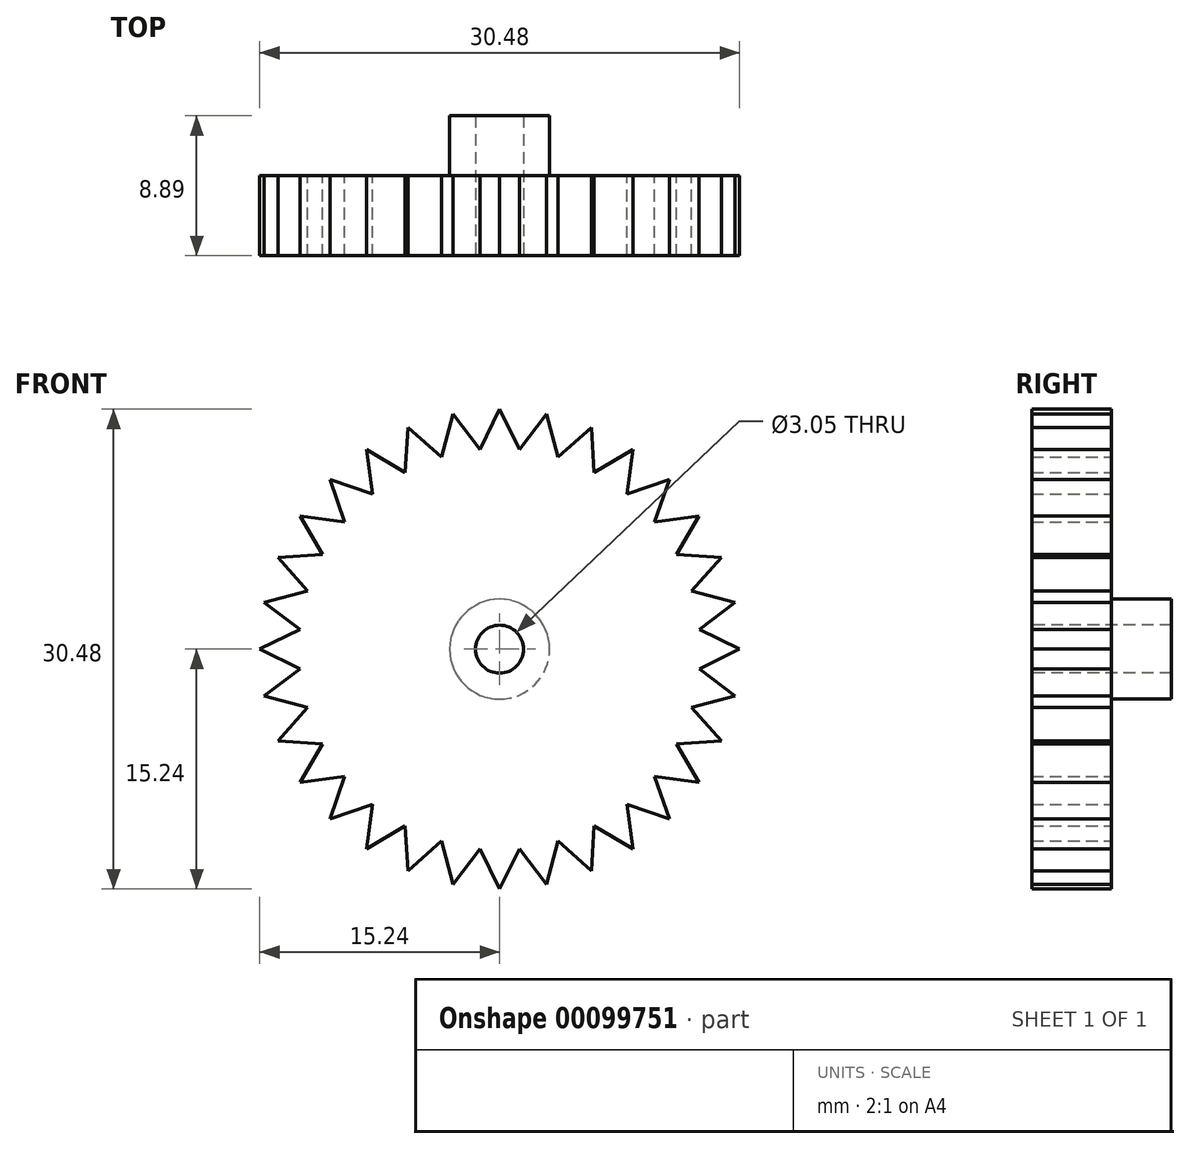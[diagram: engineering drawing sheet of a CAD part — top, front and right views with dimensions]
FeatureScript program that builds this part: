
annotation { "Feature Type Name" : "Feature", "Feature Type Description" : "" }
export const myFeature = defineFeature(function(context is Context, id is Id, definition is map)
    precondition{}
    {
        {
            var Q0;
            Q0=qCreatedBy(makeId("Front.planeOp"),FACE);
            var sketch = newSketch(context, id + "F0", { "sketchPlane" : qUnion([Q0])});
            skCircle(sketch, "E0", {"center": v(0, 0) * mm, "radius": 12.7 * mm});
            skLineSegment(sketch, "E1", {"start": v(1.27, 12.64) * mm, "end": v(0, 15.24) * mm});
            skLineSegment(sketch, "E2", {"start": v(0, 15.24) * mm, "end": v(-1.27, 12.64) * mm});
            skLineSegment(sketch, "E3.1.0", {"start": v(-2.97, 14.95) * mm, "end": v(-3.71, 12.15) * mm});
            skLineSegment(sketch, "E3.1.1", {"start": v(-1.22, 12.64) * mm, "end": v(-2.97, 14.95) * mm});
            skLineSegment(sketch, "E3.2.0", {"start": v(-5.83, 14.08) * mm, "end": v(-6, 11.19) * mm});
            skLineSegment(sketch, "E3.2.1", {"start": v(-3.66, 12.16) * mm, "end": v(-5.83, 14.08) * mm});
            skLineSegment(sketch, "E4.2.3.0", {"start": v(-8.47, 12.67) * mm, "end": v(-8.08, 9.8) * mm});
            skLineSegment(sketch, "E4.3.3.0", {"start": v(-5.96, 11.21) * mm, "end": v(-8.47, 12.67) * mm});
            skLineSegment(sketch, "E4.2.4.0", {"start": v(-10.78, 10.78) * mm, "end": v(-9.83, 8.04) * mm});
            skLineSegment(sketch, "E4.3.4.0", {"start": v(-8.04, 9.83) * mm, "end": v(-10.78, 10.78) * mm});
            skLineSegment(sketch, "E4.2.5.0", {"start": v(-12.67, 8.47) * mm, "end": v(-11.21, 5.96) * mm});
            skLineSegment(sketch, "E4.3.5.0", {"start": v(-9.8, 8.08) * mm, "end": v(-12.67, 8.47) * mm});
            skLineSegment(sketch, "E4.2.6.0", {"start": v(-14.08, 5.83) * mm, "end": v(-12.16, 3.66) * mm});
            skLineSegment(sketch, "E4.3.6.0", {"start": v(-11.19, 6) * mm, "end": v(-14.08, 5.83) * mm});
            skLineSegment(sketch, "E4.2.7.0", {"start": v(-14.95, 2.97) * mm, "end": v(-12.64, 1.22) * mm});
            skLineSegment(sketch, "E4.3.7.0", {"start": v(-12.15, 3.71) * mm, "end": v(-14.95, 2.97) * mm});
            skLineSegment(sketch, "E4.2.8.0", {"start": v(-15.24, 0) * mm, "end": v(-12.64, -1.27) * mm});
            skLineSegment(sketch, "E4.3.8.0", {"start": v(-12.64, 1.27) * mm, "end": v(-15.24, 0) * mm});
            skLineSegment(sketch, "E4.2.9.0", {"start": v(-14.95, -2.97) * mm, "end": v(-12.15, -3.71) * mm});
            skLineSegment(sketch, "E4.3.9.0", {"start": v(-12.64, -1.22) * mm, "end": v(-14.95, -2.97) * mm});
            skLineSegment(sketch, "E4.2.10.0", {"start": v(-14.08, -5.83) * mm, "end": v(-11.19, -6) * mm});
            skLineSegment(sketch, "E4.3.10.0", {"start": v(-12.16, -3.66) * mm, "end": v(-14.08, -5.83) * mm});
            skLineSegment(sketch, "E4.2.11.0", {"start": v(-12.67, -8.47) * mm, "end": v(-9.8, -8.08) * mm});
            skLineSegment(sketch, "E4.3.11.0", {"start": v(-11.21, -5.96) * mm, "end": v(-12.67, -8.47) * mm});
            skLineSegment(sketch, "E4.2.12.0", {"start": v(-10.78, -10.78) * mm, "end": v(-8.04, -9.83) * mm});
            skLineSegment(sketch, "E4.3.12.0", {"start": v(-9.83, -8.04) * mm, "end": v(-10.78, -10.78) * mm});
            skLineSegment(sketch, "E4.2.13.0", {"start": v(-8.47, -12.67) * mm, "end": v(-5.96, -11.21) * mm});
            skLineSegment(sketch, "E4.3.13.0", {"start": v(-8.08, -9.8) * mm, "end": v(-8.47, -12.67) * mm});
            skLineSegment(sketch, "E4.2.14.0", {"start": v(-5.83, -14.08) * mm, "end": v(-3.66, -12.16) * mm});
            skLineSegment(sketch, "E4.3.14.0", {"start": v(-6, -11.19) * mm, "end": v(-5.83, -14.08) * mm});
            skLineSegment(sketch, "E4.2.15.0", {"start": v(-2.97, -14.95) * mm, "end": v(-1.22, -12.64) * mm});
            skLineSegment(sketch, "E4.3.15.0", {"start": v(-3.71, -12.15) * mm, "end": v(-2.97, -14.95) * mm});
            skLineSegment(sketch, "E4.2.16.0", {"start": v(0, -15.24) * mm, "end": v(1.27, -12.64) * mm});
            skLineSegment(sketch, "E4.3.16.0", {"start": v(-1.27, -12.64) * mm, "end": v(0, -15.24) * mm});
            skLineSegment(sketch, "E4.2.17.0", {"start": v(2.97, -14.95) * mm, "end": v(3.71, -12.15) * mm});
            skLineSegment(sketch, "E4.3.17.0", {"start": v(1.22, -12.64) * mm, "end": v(2.97, -14.95) * mm});
            skLineSegment(sketch, "E4.2.18.0", {"start": v(5.83, -14.08) * mm, "end": v(6, -11.19) * mm});
            skLineSegment(sketch, "E4.3.18.0", {"start": v(3.66, -12.16) * mm, "end": v(5.83, -14.08) * mm});
            skLineSegment(sketch, "E4.2.19.0", {"start": v(8.47, -12.67) * mm, "end": v(8.08, -9.8) * mm});
            skLineSegment(sketch, "E4.3.19.0", {"start": v(5.96, -11.21) * mm, "end": v(8.47, -12.67) * mm});
            skLineSegment(sketch, "E4.2.20.0", {"start": v(10.78, -10.78) * mm, "end": v(9.83, -8.04) * mm});
            skLineSegment(sketch, "E4.3.20.0", {"start": v(8.04, -9.83) * mm, "end": v(10.78, -10.78) * mm});
            skLineSegment(sketch, "E4.2.21.0", {"start": v(12.67, -8.47) * mm, "end": v(11.21, -5.96) * mm});
            skLineSegment(sketch, "E4.3.21.0", {"start": v(9.8, -8.08) * mm, "end": v(12.67, -8.47) * mm});
            skLineSegment(sketch, "E4.2.22.0", {"start": v(14.08, -5.83) * mm, "end": v(12.16, -3.66) * mm});
            skLineSegment(sketch, "E4.3.22.0", {"start": v(11.19, -6) * mm, "end": v(14.08, -5.83) * mm});
            skLineSegment(sketch, "E4.2.23.0", {"start": v(14.95, -2.97) * mm, "end": v(12.64, -1.22) * mm});
            skLineSegment(sketch, "E4.3.23.0", {"start": v(12.15, -3.71) * mm, "end": v(14.95, -2.97) * mm});
            skLineSegment(sketch, "E4.2.24.0", {"start": v(15.24, 0) * mm, "end": v(12.64, 1.27) * mm});
            skLineSegment(sketch, "E4.3.24.0", {"start": v(12.64, -1.27) * mm, "end": v(15.24, 0) * mm});
            skLineSegment(sketch, "E4.2.25.0", {"start": v(14.95, 2.97) * mm, "end": v(12.15, 3.71) * mm});
            skLineSegment(sketch, "E4.3.25.0", {"start": v(12.64, 1.22) * mm, "end": v(14.95, 2.97) * mm});
            skLineSegment(sketch, "E4.2.26.0", {"start": v(14.08, 5.83) * mm, "end": v(11.19, 6) * mm});
            skLineSegment(sketch, "E4.3.26.0", {"start": v(12.16, 3.66) * mm, "end": v(14.08, 5.83) * mm});
            skLineSegment(sketch, "E4.2.27.0", {"start": v(12.67, 8.47) * mm, "end": v(9.8, 8.08) * mm});
            skLineSegment(sketch, "E4.3.27.0", {"start": v(11.21, 5.96) * mm, "end": v(12.67, 8.47) * mm});
            skLineSegment(sketch, "E4.2.28.0", {"start": v(10.78, 10.78) * mm, "end": v(8.04, 9.83) * mm});
            skLineSegment(sketch, "E4.3.28.0", {"start": v(9.83, 8.04) * mm, "end": v(10.78, 10.78) * mm});
            skLineSegment(sketch, "E4.2.29.0", {"start": v(8.47, 12.67) * mm, "end": v(5.96, 11.21) * mm});
            skLineSegment(sketch, "E4.3.29.0", {"start": v(8.08, 9.8) * mm, "end": v(8.47, 12.67) * mm});
            skLineSegment(sketch, "E4.2.30.0", {"start": v(5.83, 14.08) * mm, "end": v(3.66, 12.16) * mm});
            skLineSegment(sketch, "E4.3.30.0", {"start": v(6, 11.19) * mm, "end": v(5.83, 14.08) * mm});
            skLineSegment(sketch, "E4.2.31.0", {"start": v(2.97, 14.95) * mm, "end": v(1.22, 12.64) * mm});
            skLineSegment(sketch, "E4.3.31.0", {"start": v(3.71, 12.15) * mm, "end": v(2.97, 14.95) * mm});
            skSolve(sketch);
        }
        {
            var Q0;
            {var subQ3=sQuery(id+"F0.wireOp",EDGE,"E3.1.0");var subQ5=sQuery(id+"F0.wireOp",EDGE,"E0");var subQ6=makeQuery(id+"F0.imprint","INTERSECT",VERTEX,{"derivedFrom":[subQ5,subQ3]});Q0=makeQuery(id+"F0.imprint","IMPRINT",FACE,{"disambiguationData":[TD([[makeQuery(id+"F0.imprint","IMPRINT",EDGE,{"disambiguationData":[TD([[subQ6,-1.0]])],"derivedFrom":subQ5}),-1.0]])]});}
            var Q1;
            {var subQ3=sQuery(id+"F0.wireOp",EDGE,"E4.2.17.0");var subQ7=sQuery(id+"F0.wireOp",EDGE,"E0");var subQ8=makeQuery(id+"F0.imprint","INTERSECT",VERTEX,{"derivedFrom":[subQ7,subQ3]});Q1=makeQuery(id+"F0.imprint","IMPRINT",FACE,{"disambiguationData":[TD([[makeQuery(id+"F0.imprint","IMPRINT",EDGE,{"disambiguationData":[TD([[subQ8,-1.0]])],"derivedFrom":subQ7}),-1.0]])]});}
            var Q2;
            {var subQ3=sQuery(id+"F0.wireOp",EDGE,"E4.2.9.0");var subQ7=sQuery(id+"F0.wireOp",EDGE,"E0");var subQ8=makeQuery(id+"F0.imprint","INTERSECT",VERTEX,{"derivedFrom":[subQ7,subQ3]});Q2=makeQuery(id+"F0.imprint","IMPRINT",FACE,{"disambiguationData":[TD([[makeQuery(id+"F0.imprint","IMPRINT",EDGE,{"disambiguationData":[TD([[subQ8,-1.0]])],"derivedFrom":subQ7}),-1.0]])]});}
            var Q3;
            {var subQ5=sQuery(id+"F0.wireOp",EDGE,"E4.2.22.0");var subQ7=sQuery(id+"F0.wireOp",EDGE,"E0");var subQ8=makeQuery(id+"F0.imprint","INTERSECT",VERTEX,{"derivedFrom":[subQ7,subQ5]});Q3=makeQuery(id+"F0.imprint","IMPRINT",FACE,{"disambiguationData":[TD([[makeQuery(id+"F0.imprint","IMPRINT",EDGE,{"disambiguationData":[TD([[subQ8,-1.0]])],"derivedFrom":subQ7}),-1.0]])]});}
            var Q4;
            {var subQ3=sQuery(id+"F0.wireOp",EDGE,"E4.2.14.0");var subQ7=sQuery(id+"F0.wireOp",EDGE,"E0");var subQ8=makeQuery(id+"F0.imprint","INTERSECT",VERTEX,{"derivedFrom":[subQ7,subQ3]});Q4=makeQuery(id+"F0.imprint","IMPRINT",FACE,{"disambiguationData":[TD([[makeQuery(id+"F0.imprint","IMPRINT",EDGE,{"disambiguationData":[TD([[subQ8,-1.0]])],"derivedFrom":subQ7}),-1.0]])]});}
            var Q5;
            {var subQ3=sQuery(id+"F0.wireOp",EDGE,"E4.2.6.0");var subQ7=sQuery(id+"F0.wireOp",EDGE,"E0");var subQ8=makeQuery(id+"F0.imprint","INTERSECT",VERTEX,{"derivedFrom":[subQ7,subQ3]});Q5=makeQuery(id+"F0.imprint","IMPRINT",FACE,{"disambiguationData":[TD([[makeQuery(id+"F0.imprint","IMPRINT",EDGE,{"disambiguationData":[TD([[subQ8,-1.0]])],"derivedFrom":subQ7}),-1.0]])]});}
            var Q6;
            {var subQ0=sQuery(id+"F0.wireOp",EDGE,"E3.1.1");var subQ1=sQuery(id+"F0.wireOp",EDGE,"E0");var subQ2=makeQuery(id+"F0.imprint","INTERSECT",VERTEX,{"derivedFrom":[subQ1,subQ0]});Q6=makeQuery(id+"F0.imprint","IMPRINT",FACE,{"disambiguationData":[TD([[makeQuery(id+"F0.imprint","IMPRINT",EDGE,{"disambiguationData":[TD([[subQ2,1.0]])],"derivedFrom":subQ1}),-1.0]])]});}
            var Q7;
            {var subQ3=sQuery(id+"F0.wireOp",EDGE,"E1");var subQ6=sQuery(id+"F0.wireOp",EDGE,"E0");var subQ9=makeQuery(id+"F0.imprint","INTERSECT",VERTEX,{"derivedFrom":[subQ6,subQ3]});Q7=makeQuery(id+"F0.imprint","IMPRINT",FACE,{"disambiguationData":[TD([[makeQuery(id+"F0.imprint","IMPRINT",EDGE,{"disambiguationData":[TD([[subQ9,1.0]])],"derivedFrom":subQ6}),-1.0]])]});}
            var Q8;
            {var subQ0=sQuery(id+"F0.wireOp",EDGE,"E0");var subQ35=makeQuery(id+"F0.imprint","INTERSECT",VERTEX,{"derivedFrom":[subQ0,sQuery(id+"F0.wireOp",EDGE,"E4.2.24.0")]});Q8=makeQuery(id+"F0.imprint","IMPRINT",FACE,{"disambiguationData":[TD([[makeQuery(id+"F0.imprint","IMPRINT",EDGE,{"disambiguationData":[TD([[subQ35,1.0]])],"derivedFrom":subQ0}),1.0]])]});}
            var Q9;
            {var subQ3=sQuery(id+"F0.wireOp",EDGE,"E4.2.24.0");var subQ7=sQuery(id+"F0.wireOp",EDGE,"E0");var subQ8=makeQuery(id+"F0.imprint","INTERSECT",VERTEX,{"derivedFrom":[subQ7,subQ3]});Q9=makeQuery(id+"F0.imprint","IMPRINT",FACE,{"disambiguationData":[TD([[makeQuery(id+"F0.imprint","IMPRINT",EDGE,{"disambiguationData":[TD([[subQ8,-1.0]])],"derivedFrom":subQ7}),-1.0]])]});}
            var Q10;
            {var subQ3=sQuery(id+"F0.wireOp",EDGE,"E4.2.25.0");var subQ5=sQuery(id+"F0.wireOp",EDGE,"E0");var subQ6=makeQuery(id+"F0.imprint","INTERSECT",VERTEX,{"derivedFrom":[subQ5,subQ3]});Q10=makeQuery(id+"F0.imprint","IMPRINT",FACE,{"disambiguationData":[TD([[makeQuery(id+"F0.imprint","IMPRINT",EDGE,{"disambiguationData":[TD([[subQ6,-1.0]])],"derivedFrom":subQ5}),-1.0]])]});}
            var Q11;
            {var subQ5=sQuery(id+"F0.wireOp",EDGE,"E4.2.26.0");var subQ7=sQuery(id+"F0.wireOp",EDGE,"E0");var subQ8=makeQuery(id+"F0.imprint","INTERSECT",VERTEX,{"derivedFrom":[subQ7,subQ5]});Q11=makeQuery(id+"F0.imprint","IMPRINT",FACE,{"disambiguationData":[TD([[makeQuery(id+"F0.imprint","IMPRINT",EDGE,{"disambiguationData":[TD([[subQ8,-1.0]])],"derivedFrom":subQ7}),-1.0]])]});}
            var Q12;
            {var subQ5=sQuery(id+"F0.wireOp",EDGE,"E4.2.27.0");var subQ6=sQuery(id+"F0.wireOp",EDGE,"E0");var subQ7=makeQuery(id+"F0.imprint","INTERSECT",VERTEX,{"derivedFrom":[subQ6,subQ5]});Q12=makeQuery(id+"F0.imprint","IMPRINT",FACE,{"disambiguationData":[TD([[makeQuery(id+"F0.imprint","IMPRINT",EDGE,{"disambiguationData":[TD([[subQ7,-1.0]])],"derivedFrom":subQ6}),-1.0]])]});}
            var Q13;
            {var subQ3=sQuery(id+"F0.wireOp",EDGE,"E4.2.28.0");var subQ7=sQuery(id+"F0.wireOp",EDGE,"E0");var subQ8=makeQuery(id+"F0.imprint","INTERSECT",VERTEX,{"derivedFrom":[subQ7,subQ3]});Q13=makeQuery(id+"F0.imprint","IMPRINT",FACE,{"disambiguationData":[TD([[makeQuery(id+"F0.imprint","IMPRINT",EDGE,{"disambiguationData":[TD([[subQ8,-1.0]])],"derivedFrom":subQ7}),-1.0]])]});}
            var Q14;
            {var subQ5=sQuery(id+"F0.wireOp",EDGE,"E4.2.29.0");var subQ6=sQuery(id+"F0.wireOp",EDGE,"E0");var subQ7=makeQuery(id+"F0.imprint","INTERSECT",VERTEX,{"derivedFrom":[subQ6,subQ5]});Q14=makeQuery(id+"F0.imprint","IMPRINT",FACE,{"disambiguationData":[TD([[makeQuery(id+"F0.imprint","IMPRINT",EDGE,{"disambiguationData":[TD([[subQ7,-1.0]])],"derivedFrom":subQ6}),-1.0]])]});}
            var Q15;
            {var subQ3=sQuery(id+"F0.wireOp",EDGE,"E4.2.21.0");var subQ7=sQuery(id+"F0.wireOp",EDGE,"E0");var subQ8=makeQuery(id+"F0.imprint","INTERSECT",VERTEX,{"derivedFrom":[subQ7,subQ3]});Q15=makeQuery(id+"F0.imprint","IMPRINT",FACE,{"disambiguationData":[TD([[makeQuery(id+"F0.imprint","IMPRINT",EDGE,{"disambiguationData":[TD([[subQ8,-1.0]])],"derivedFrom":subQ7}),-1.0]])]});}
            var Q16;
            {var subQ3=sQuery(id+"F0.wireOp",EDGE,"E4.2.13.0");var subQ5=sQuery(id+"F0.wireOp",EDGE,"E0");var subQ6=makeQuery(id+"F0.imprint","INTERSECT",VERTEX,{"derivedFrom":[subQ5,subQ3]});Q16=makeQuery(id+"F0.imprint","IMPRINT",FACE,{"disambiguationData":[TD([[makeQuery(id+"F0.imprint","IMPRINT",EDGE,{"disambiguationData":[TD([[subQ6,-1.0]])],"derivedFrom":subQ5}),-1.0]])]});}
            var Q17;
            {var subQ3=sQuery(id+"F0.wireOp",EDGE,"E4.2.5.0");var subQ5=sQuery(id+"F0.wireOp",EDGE,"E0");var subQ6=makeQuery(id+"F0.imprint","INTERSECT",VERTEX,{"derivedFrom":[subQ5,subQ3]});Q17=makeQuery(id+"F0.imprint","IMPRINT",FACE,{"disambiguationData":[TD([[makeQuery(id+"F0.imprint","IMPRINT",EDGE,{"disambiguationData":[TD([[subQ6,-1.0]])],"derivedFrom":subQ5}),-1.0]])]});}
            var Q18;
            {var subQ3=sQuery(id+"F0.wireOp",EDGE,"E4.2.19.0");var subQ5=sQuery(id+"F0.wireOp",EDGE,"E0");var subQ6=makeQuery(id+"F0.imprint","INTERSECT",VERTEX,{"derivedFrom":[subQ5,subQ3]});Q18=makeQuery(id+"F0.imprint","IMPRINT",FACE,{"disambiguationData":[TD([[makeQuery(id+"F0.imprint","IMPRINT",EDGE,{"disambiguationData":[TD([[subQ6,-1.0]])],"derivedFrom":subQ5}),-1.0]])]});}
            var Q19;
            {var subQ5=sQuery(id+"F0.wireOp",EDGE,"E4.2.11.0");var subQ6=sQuery(id+"F0.wireOp",EDGE,"E0");var subQ7=makeQuery(id+"F0.imprint","INTERSECT",VERTEX,{"derivedFrom":[subQ6,subQ5]});Q19=makeQuery(id+"F0.imprint","IMPRINT",FACE,{"disambiguationData":[TD([[makeQuery(id+"F0.imprint","IMPRINT",EDGE,{"disambiguationData":[TD([[subQ7,-1.0]])],"derivedFrom":subQ6}),-1.0]])]});}
            var Q20;
            {var subQ5=sQuery(id+"F0.wireOp",EDGE,"E4.2.3.0");var subQ6=sQuery(id+"F0.wireOp",EDGE,"E0");var subQ7=makeQuery(id+"F0.imprint","INTERSECT",VERTEX,{"derivedFrom":[subQ6,subQ5]});Q20=makeQuery(id+"F0.imprint","IMPRINT",FACE,{"disambiguationData":[TD([[makeQuery(id+"F0.imprint","IMPRINT",EDGE,{"disambiguationData":[TD([[subQ7,-1.0]])],"derivedFrom":subQ6}),-1.0]])]});}
            var Q21;
            {var subQ3=sQuery(id+"F0.wireOp",EDGE,"E3.2.0");var subQ7=sQuery(id+"F0.wireOp",EDGE,"E0");var subQ9=makeQuery(id+"F0.imprint","INTERSECT",VERTEX,{"derivedFrom":[subQ7,subQ3]});Q21=makeQuery(id+"F0.imprint","IMPRINT",FACE,{"disambiguationData":[TD([[makeQuery(id+"F0.imprint","IMPRINT",EDGE,{"disambiguationData":[TD([[subQ9,-1.0]])],"derivedFrom":subQ7}),-1.0]])]});}
            var Q22;
            {var subQ3=sQuery(id+"F0.wireOp",EDGE,"E4.2.18.0");var subQ7=sQuery(id+"F0.wireOp",EDGE,"E0");var subQ8=makeQuery(id+"F0.imprint","INTERSECT",VERTEX,{"derivedFrom":[subQ7,subQ3]});Q22=makeQuery(id+"F0.imprint","IMPRINT",FACE,{"disambiguationData":[TD([[makeQuery(id+"F0.imprint","IMPRINT",EDGE,{"disambiguationData":[TD([[subQ8,-1.0]])],"derivedFrom":subQ7}),-1.0]])]});}
            var Q23;
            {var subQ3=sQuery(id+"F0.wireOp",EDGE,"E4.2.10.0");var subQ7=sQuery(id+"F0.wireOp",EDGE,"E0");var subQ8=makeQuery(id+"F0.imprint","INTERSECT",VERTEX,{"derivedFrom":[subQ7,subQ3]});Q23=makeQuery(id+"F0.imprint","IMPRINT",FACE,{"disambiguationData":[TD([[makeQuery(id+"F0.imprint","IMPRINT",EDGE,{"disambiguationData":[TD([[subQ8,-1.0]])],"derivedFrom":subQ7}),-1.0]])]});}
            var Q24;
            {var subQ0=sQuery(id+"F0.wireOp",EDGE,"E2");var subQ1=sQuery(id+"F0.wireOp",EDGE,"E0");var subQ2=makeQuery(id+"F0.imprint","INTERSECT",VERTEX,{"derivedFrom":[subQ1,subQ0]});Q24=makeQuery(id+"F0.imprint","IMPRINT",FACE,{"disambiguationData":[TD([[makeQuery(id+"F0.imprint","IMPRINT",EDGE,{"disambiguationData":[TD([[subQ2,-1.0]])],"derivedFrom":subQ1}),-1.0]])]});}
            var Q25;
            {var subQ0=sQuery(id+"F0.wireOp",EDGE,"E4.2.16.0");var subQ1=sQuery(id+"F0.wireOp",EDGE,"E0");var subQ2=makeQuery(id+"F0.imprint","INTERSECT",VERTEX,{"derivedFrom":[subQ1,subQ0]});Q25=makeQuery(id+"F0.imprint","IMPRINT",FACE,{"disambiguationData":[TD([[makeQuery(id+"F0.imprint","IMPRINT",EDGE,{"disambiguationData":[TD([[subQ2,-1.0]])],"derivedFrom":subQ1}),-1.0]])]});}
            var Q26;
            {var subQ3=sQuery(id+"F0.wireOp",EDGE,"E4.2.8.0");var subQ5=sQuery(id+"F0.wireOp",EDGE,"E0");var subQ6=makeQuery(id+"F0.imprint","INTERSECT",VERTEX,{"derivedFrom":[subQ5,subQ3]});Q26=makeQuery(id+"F0.imprint","IMPRINT",FACE,{"disambiguationData":[TD([[makeQuery(id+"F0.imprint","IMPRINT",EDGE,{"disambiguationData":[TD([[subQ6,-1.0]])],"derivedFrom":subQ5}),-1.0]])]});}
            var Q27;
            {var subQ3=sQuery(id+"F0.wireOp",EDGE,"E4.2.7.0");var subQ7=sQuery(id+"F0.wireOp",EDGE,"E0");var subQ8=makeQuery(id+"F0.imprint","INTERSECT",VERTEX,{"derivedFrom":[subQ7,subQ3]});Q27=makeQuery(id+"F0.imprint","IMPRINT",FACE,{"disambiguationData":[TD([[makeQuery(id+"F0.imprint","IMPRINT",EDGE,{"disambiguationData":[TD([[subQ8,-1.0]])],"derivedFrom":subQ7}),-1.0]])]});}
            var Q28;
            {var subQ5=sQuery(id+"F0.wireOp",EDGE,"E4.2.20.0");var subQ6=sQuery(id+"F0.wireOp",EDGE,"E0");var subQ7=makeQuery(id+"F0.imprint","INTERSECT",VERTEX,{"derivedFrom":[subQ6,subQ5]});Q28=makeQuery(id+"F0.imprint","IMPRINT",FACE,{"disambiguationData":[TD([[makeQuery(id+"F0.imprint","IMPRINT",EDGE,{"disambiguationData":[TD([[subQ7,-1.0]])],"derivedFrom":subQ6}),-1.0]])]});}
            var Q29;
            {var subQ3=sQuery(id+"F0.wireOp",EDGE,"E4.2.12.0");var subQ7=sQuery(id+"F0.wireOp",EDGE,"E0");var subQ8=makeQuery(id+"F0.imprint","INTERSECT",VERTEX,{"derivedFrom":[subQ7,subQ3]});Q29=makeQuery(id+"F0.imprint","IMPRINT",FACE,{"disambiguationData":[TD([[makeQuery(id+"F0.imprint","IMPRINT",EDGE,{"disambiguationData":[TD([[subQ8,-1.0]])],"derivedFrom":subQ7}),-1.0]])]});}
            var Q30;
            {var subQ5=sQuery(id+"F0.wireOp",EDGE,"E0");var subQ7=sQuery(id+"F0.wireOp",EDGE,"E4.2.4.0");var subQ9=makeQuery(id+"F0.imprint","INTERSECT",VERTEX,{"derivedFrom":[subQ5,subQ7]});Q30=makeQuery(id+"F0.imprint","IMPRINT",FACE,{"disambiguationData":[TD([[makeQuery(id+"F0.imprint","IMPRINT",EDGE,{"disambiguationData":[TD([[subQ9,-1.0]])],"derivedFrom":subQ5}),-1.0]])]});}
            var Q31;
            {var subQ3=sQuery(id+"F0.wireOp",EDGE,"E4.2.15.0");var subQ7=sQuery(id+"F0.wireOp",EDGE,"E0");var subQ8=makeQuery(id+"F0.imprint","INTERSECT",VERTEX,{"derivedFrom":[subQ7,subQ3]});Q31=makeQuery(id+"F0.imprint","IMPRINT",FACE,{"disambiguationData":[TD([[makeQuery(id+"F0.imprint","IMPRINT",EDGE,{"disambiguationData":[TD([[subQ8,-1.0]])],"derivedFrom":subQ7}),-1.0]])]});}
            var Q32;
            {var subQ0=sQuery(id+"F0.wireOp",EDGE,"E4.2.19.0");var subQ1=sQuery(id+"F0.wireOp",EDGE,"E0");var subQ2=makeQuery(id+"F0.imprint","INTERSECT",VERTEX,{"derivedFrom":[subQ1,subQ0]});Q32=makeQuery(id+"F0.imprint","IMPRINT",FACE,{"disambiguationData":[TD([[makeQuery(id+"F0.imprint","IMPRINT",EDGE,{"disambiguationData":[TD([[subQ2,1.0]])],"derivedFrom":subQ1}),-1.0]])]});}
            var Q33;
            {var subQ0=sQuery(id+"F0.wireOp",EDGE,"E4.2.28.0");var subQ1=sQuery(id+"F0.wireOp",EDGE,"E0");var subQ2=makeQuery(id+"F0.imprint","INTERSECT",VERTEX,{"derivedFrom":[subQ1,subQ0]});Q33=makeQuery(id+"F0.imprint","IMPRINT",FACE,{"disambiguationData":[TD([[makeQuery(id+"F0.imprint","IMPRINT",EDGE,{"disambiguationData":[TD([[subQ2,1.0]])],"derivedFrom":subQ1}),-1.0]])]});}
            var Q34;
            {var subQ3=sQuery(id+"F0.wireOp",EDGE,"E4.2.23.0");var subQ7=sQuery(id+"F0.wireOp",EDGE,"E0");var subQ8=makeQuery(id+"F0.imprint","INTERSECT",VERTEX,{"derivedFrom":[subQ7,subQ3]});Q34=makeQuery(id+"F0.imprint","IMPRINT",FACE,{"disambiguationData":[TD([[makeQuery(id+"F0.imprint","IMPRINT",EDGE,{"disambiguationData":[TD([[subQ8,-1.0]])],"derivedFrom":subQ7}),-1.0]])]});}
            var Q35;
            {var subQ0=sQuery(id+"F0.wireOp",EDGE,"E4.2.21.0");var subQ1=sQuery(id+"F0.wireOp",EDGE,"E0");var subQ2=makeQuery(id+"F0.imprint","INTERSECT",VERTEX,{"derivedFrom":[subQ1,subQ0]});Q35=makeQuery(id+"F0.imprint","IMPRINT",FACE,{"disambiguationData":[TD([[makeQuery(id+"F0.imprint","IMPRINT",EDGE,{"disambiguationData":[TD([[subQ2,1.0]])],"derivedFrom":subQ1}),-1.0]])]});}
            var Q36;
            {var subQ0=sQuery(id+"F0.wireOp",EDGE,"E4.2.13.0");var subQ1=sQuery(id+"F0.wireOp",EDGE,"E0");var subQ2=makeQuery(id+"F0.imprint","INTERSECT",VERTEX,{"derivedFrom":[subQ1,subQ0]});Q36=makeQuery(id+"F0.imprint","IMPRINT",FACE,{"disambiguationData":[TD([[makeQuery(id+"F0.imprint","IMPRINT",EDGE,{"disambiguationData":[TD([[subQ2,1.0]])],"derivedFrom":subQ1}),-1.0]])]});}
            var Q37;
            {var subQ0=sQuery(id+"F0.wireOp",EDGE,"E4.2.5.0");var subQ1=sQuery(id+"F0.wireOp",EDGE,"E0");var subQ2=makeQuery(id+"F0.imprint","INTERSECT",VERTEX,{"derivedFrom":[subQ1,subQ0]});Q37=makeQuery(id+"F0.imprint","IMPRINT",FACE,{"disambiguationData":[TD([[makeQuery(id+"F0.imprint","IMPRINT",EDGE,{"disambiguationData":[TD([[subQ2,1.0]])],"derivedFrom":subQ1}),-1.0]])]});}
            var Q38;
            {var subQ0=sQuery(id+"F0.wireOp",EDGE,"E4.2.11.0");var subQ1=sQuery(id+"F0.wireOp",EDGE,"E0");var subQ2=makeQuery(id+"F0.imprint","INTERSECT",VERTEX,{"derivedFrom":[subQ1,subQ0]});Q38=makeQuery(id+"F0.imprint","IMPRINT",FACE,{"disambiguationData":[TD([[makeQuery(id+"F0.imprint","IMPRINT",EDGE,{"disambiguationData":[TD([[subQ2,1.0]])],"derivedFrom":subQ1}),-1.0]])]});}
            var Q39;
            {var subQ0=sQuery(id+"F0.wireOp",EDGE,"E4.2.3.0");var subQ1=sQuery(id+"F0.wireOp",EDGE,"E0");var subQ2=makeQuery(id+"F0.imprint","INTERSECT",VERTEX,{"derivedFrom":[subQ1,subQ0]});Q39=makeQuery(id+"F0.imprint","IMPRINT",FACE,{"disambiguationData":[TD([[makeQuery(id+"F0.imprint","IMPRINT",EDGE,{"disambiguationData":[TD([[subQ2,1.0]])],"derivedFrom":subQ1}),-1.0]])]});}
            var Q40;
            {var subQ0=sQuery(id+"F0.wireOp",EDGE,"E3.2.0");var subQ1=sQuery(id+"F0.wireOp",EDGE,"E0");var subQ2=makeQuery(id+"F0.imprint","INTERSECT",VERTEX,{"derivedFrom":[subQ1,subQ0]});Q40=makeQuery(id+"F0.imprint","IMPRINT",FACE,{"disambiguationData":[TD([[makeQuery(id+"F0.imprint","IMPRINT",EDGE,{"disambiguationData":[TD([[subQ2,1.0]])],"derivedFrom":subQ1}),-1.0]])]});}
            var Q41;
            {var subQ0=sQuery(id+"F0.wireOp",EDGE,"E4.2.18.0");var subQ1=sQuery(id+"F0.wireOp",EDGE,"E0");var subQ2=makeQuery(id+"F0.imprint","INTERSECT",VERTEX,{"derivedFrom":[subQ1,subQ0]});Q41=makeQuery(id+"F0.imprint","IMPRINT",FACE,{"disambiguationData":[TD([[makeQuery(id+"F0.imprint","IMPRINT",EDGE,{"disambiguationData":[TD([[subQ2,1.0]])],"derivedFrom":subQ1}),-1.0]])]});}
            var Q42;
            {var subQ0=sQuery(id+"F0.wireOp",EDGE,"E4.2.10.0");var subQ1=sQuery(id+"F0.wireOp",EDGE,"E0");var subQ2=makeQuery(id+"F0.imprint","INTERSECT",VERTEX,{"derivedFrom":[subQ1,subQ0]});Q42=makeQuery(id+"F0.imprint","IMPRINT",FACE,{"disambiguationData":[TD([[makeQuery(id+"F0.imprint","IMPRINT",EDGE,{"disambiguationData":[TD([[subQ2,1.0]])],"derivedFrom":subQ1}),-1.0]])]});}
            var Q43;
            {var subQ0=sQuery(id+"F0.wireOp",EDGE,"E2");var subQ1=sQuery(id+"F0.wireOp",EDGE,"E0");var subQ2=makeQuery(id+"F0.imprint","INTERSECT",VERTEX,{"derivedFrom":[subQ1,subQ0]});Q43=makeQuery(id+"F0.imprint","IMPRINT",FACE,{"disambiguationData":[TD([[makeQuery(id+"F0.imprint","IMPRINT",EDGE,{"disambiguationData":[TD([[subQ2,1.0]])],"derivedFrom":subQ1}),-1.0]])]});}
            var Q44;
            {var subQ0=sQuery(id+"F0.wireOp",EDGE,"E4.2.24.0");var subQ1=sQuery(id+"F0.wireOp",EDGE,"E0");var subQ2=makeQuery(id+"F0.imprint","INTERSECT",VERTEX,{"derivedFrom":[subQ1,subQ0]});Q44=makeQuery(id+"F0.imprint","IMPRINT",FACE,{"disambiguationData":[TD([[makeQuery(id+"F0.imprint","IMPRINT",EDGE,{"disambiguationData":[TD([[subQ2,1.0]])],"derivedFrom":subQ1}),-1.0]])]});}
            var Q45;
            {var subQ0=sQuery(id+"F0.wireOp",EDGE,"E4.2.23.0");var subQ1=sQuery(id+"F0.wireOp",EDGE,"E0");var subQ2=makeQuery(id+"F0.imprint","INTERSECT",VERTEX,{"derivedFrom":[subQ1,subQ0]});Q45=makeQuery(id+"F0.imprint","IMPRINT",FACE,{"disambiguationData":[TD([[makeQuery(id+"F0.imprint","IMPRINT",EDGE,{"disambiguationData":[TD([[subQ2,1.0]])],"derivedFrom":subQ1}),-1.0]])]});}
            var Q46;
            {var subQ0=sQuery(id+"F0.wireOp",EDGE,"E4.2.7.0");var subQ1=sQuery(id+"F0.wireOp",EDGE,"E0");var subQ2=makeQuery(id+"F0.imprint","INTERSECT",VERTEX,{"derivedFrom":[subQ1,subQ0]});Q46=makeQuery(id+"F0.imprint","IMPRINT",FACE,{"disambiguationData":[TD([[makeQuery(id+"F0.imprint","IMPRINT",EDGE,{"disambiguationData":[TD([[subQ2,1.0]])],"derivedFrom":subQ1}),-1.0]])]});}
            var Q47;
            {var subQ0=sQuery(id+"F0.wireOp",EDGE,"E4.2.22.0");var subQ1=sQuery(id+"F0.wireOp",EDGE,"E0");var subQ2=makeQuery(id+"F0.imprint","INTERSECT",VERTEX,{"derivedFrom":[subQ1,subQ0]});Q47=makeQuery(id+"F0.imprint","IMPRINT",FACE,{"disambiguationData":[TD([[makeQuery(id+"F0.imprint","IMPRINT",EDGE,{"disambiguationData":[TD([[subQ2,1.0]])],"derivedFrom":subQ1}),-1.0]])]});}
            var Q48;
            {var subQ0=sQuery(id+"F0.wireOp",EDGE,"E4.2.6.0");var subQ1=sQuery(id+"F0.wireOp",EDGE,"E0");var subQ2=makeQuery(id+"F0.imprint","INTERSECT",VERTEX,{"derivedFrom":[subQ1,subQ0]});Q48=makeQuery(id+"F0.imprint","IMPRINT",FACE,{"disambiguationData":[TD([[makeQuery(id+"F0.imprint","IMPRINT",EDGE,{"disambiguationData":[TD([[subQ2,1.0]])],"derivedFrom":subQ1}),-1.0]])]});}
            var Q49;
            {var subQ0=sQuery(id+"F0.wireOp",EDGE,"E4.2.20.0");var subQ1=sQuery(id+"F0.wireOp",EDGE,"E0");var subQ2=makeQuery(id+"F0.imprint","INTERSECT",VERTEX,{"derivedFrom":[subQ1,subQ0]});Q49=makeQuery(id+"F0.imprint","IMPRINT",FACE,{"disambiguationData":[TD([[makeQuery(id+"F0.imprint","IMPRINT",EDGE,{"disambiguationData":[TD([[subQ2,1.0]])],"derivedFrom":subQ1}),-1.0]])]});}
            var Q50;
            {var subQ0=sQuery(id+"F0.wireOp",EDGE,"E4.2.12.0");var subQ1=sQuery(id+"F0.wireOp",EDGE,"E0");var subQ2=makeQuery(id+"F0.imprint","INTERSECT",VERTEX,{"derivedFrom":[subQ1,subQ0]});Q50=makeQuery(id+"F0.imprint","IMPRINT",FACE,{"disambiguationData":[TD([[makeQuery(id+"F0.imprint","IMPRINT",EDGE,{"disambiguationData":[TD([[subQ2,1.0]])],"derivedFrom":subQ1}),-1.0]])]});}
            var Q51;
            {var subQ0=sQuery(id+"F0.wireOp",EDGE,"E4.2.4.0");var subQ1=sQuery(id+"F0.wireOp",EDGE,"E0");var subQ2=makeQuery(id+"F0.imprint","INTERSECT",VERTEX,{"derivedFrom":[subQ1,subQ0]});Q51=makeQuery(id+"F0.imprint","IMPRINT",FACE,{"disambiguationData":[TD([[makeQuery(id+"F0.imprint","IMPRINT",EDGE,{"disambiguationData":[TD([[subQ2,1.0]])],"derivedFrom":subQ1}),-1.0]])]});}
            var Q52;
            {var subQ0=sQuery(id+"F0.wireOp",EDGE,"E3.1.0");var subQ1=sQuery(id+"F0.wireOp",EDGE,"E0");var subQ2=makeQuery(id+"F0.imprint","INTERSECT",VERTEX,{"derivedFrom":[subQ1,subQ0]});Q52=makeQuery(id+"F0.imprint","IMPRINT",FACE,{"disambiguationData":[TD([[makeQuery(id+"F0.imprint","IMPRINT",EDGE,{"disambiguationData":[TD([[subQ2,1.0]])],"derivedFrom":subQ1}),-1.0]])]});}
            var Q53;
            {var subQ0=sQuery(id+"F0.wireOp",EDGE,"E4.2.17.0");var subQ1=sQuery(id+"F0.wireOp",EDGE,"E0");var subQ2=makeQuery(id+"F0.imprint","INTERSECT",VERTEX,{"derivedFrom":[subQ1,subQ0]});Q53=makeQuery(id+"F0.imprint","IMPRINT",FACE,{"disambiguationData":[TD([[makeQuery(id+"F0.imprint","IMPRINT",EDGE,{"disambiguationData":[TD([[subQ2,1.0]])],"derivedFrom":subQ1}),-1.0]])]});}
            var Q54;
            {var subQ0=sQuery(id+"F0.wireOp",EDGE,"E1");var subQ1=sQuery(id+"F0.wireOp",EDGE,"E0");var subQ2=makeQuery(id+"F0.imprint","INTERSECT",VERTEX,{"derivedFrom":[subQ1,subQ0]});Q54=makeQuery(id+"F0.imprint","IMPRINT",FACE,{"disambiguationData":[TD([[makeQuery(id+"F0.imprint","IMPRINT",EDGE,{"disambiguationData":[TD([[subQ2,-1.0]])],"derivedFrom":subQ1}),-1.0]])]});}
            var Q55;
            {var subQ0=sQuery(id+"F0.wireOp",EDGE,"E4.2.16.0");var subQ1=sQuery(id+"F0.wireOp",EDGE,"E0");var subQ2=makeQuery(id+"F0.imprint","INTERSECT",VERTEX,{"derivedFrom":[subQ1,subQ0]});Q55=makeQuery(id+"F0.imprint","IMPRINT",FACE,{"disambiguationData":[TD([[makeQuery(id+"F0.imprint","IMPRINT",EDGE,{"disambiguationData":[TD([[subQ2,1.0]])],"derivedFrom":subQ1}),-1.0]])]});}
            var Q56;
            {var subQ0=sQuery(id+"F0.wireOp",EDGE,"E4.2.8.0");var subQ1=sQuery(id+"F0.wireOp",EDGE,"E0");var subQ2=makeQuery(id+"F0.imprint","INTERSECT",VERTEX,{"derivedFrom":[subQ1,subQ0]});Q56=makeQuery(id+"F0.imprint","IMPRINT",FACE,{"disambiguationData":[TD([[makeQuery(id+"F0.imprint","IMPRINT",EDGE,{"disambiguationData":[TD([[subQ2,1.0]])],"derivedFrom":subQ1}),-1.0]])]});}
            var Q57;
            {var subQ0=sQuery(id+"F0.wireOp",EDGE,"E4.2.25.0");var subQ1=sQuery(id+"F0.wireOp",EDGE,"E0");var subQ2=makeQuery(id+"F0.imprint","INTERSECT",VERTEX,{"derivedFrom":[subQ1,subQ0]});Q57=makeQuery(id+"F0.imprint","IMPRINT",FACE,{"disambiguationData":[TD([[makeQuery(id+"F0.imprint","IMPRINT",EDGE,{"disambiguationData":[TD([[subQ2,1.0]])],"derivedFrom":subQ1}),-1.0]])]});}
            var Q58;
            {var subQ0=sQuery(id+"F0.wireOp",EDGE,"E4.2.26.0");var subQ1=sQuery(id+"F0.wireOp",EDGE,"E0");var subQ2=makeQuery(id+"F0.imprint","INTERSECT",VERTEX,{"derivedFrom":[subQ1,subQ0]});Q58=makeQuery(id+"F0.imprint","IMPRINT",FACE,{"disambiguationData":[TD([[makeQuery(id+"F0.imprint","IMPRINT",EDGE,{"disambiguationData":[TD([[subQ2,1.0]])],"derivedFrom":subQ1}),-1.0]])]});}
            var Q59;
            {var subQ0=sQuery(id+"F0.wireOp",EDGE,"E4.2.27.0");var subQ1=sQuery(id+"F0.wireOp",EDGE,"E0");var subQ2=makeQuery(id+"F0.imprint","INTERSECT",VERTEX,{"derivedFrom":[subQ1,subQ0]});Q59=makeQuery(id+"F0.imprint","IMPRINT",FACE,{"disambiguationData":[TD([[makeQuery(id+"F0.imprint","IMPRINT",EDGE,{"disambiguationData":[TD([[subQ2,1.0]])],"derivedFrom":subQ1}),-1.0]])]});}
            var Q60;
            {var subQ0=sQuery(id+"F0.wireOp",EDGE,"E4.2.29.0");var subQ1=sQuery(id+"F0.wireOp",EDGE,"E0");var subQ2=makeQuery(id+"F0.imprint","INTERSECT",VERTEX,{"derivedFrom":[subQ1,subQ0]});Q60=makeQuery(id+"F0.imprint","IMPRINT",FACE,{"disambiguationData":[TD([[makeQuery(id+"F0.imprint","IMPRINT",EDGE,{"disambiguationData":[TD([[subQ2,1.0]])],"derivedFrom":subQ1}),-1.0]])]});}
            var Q61;
            {var subQ0=sQuery(id+"F0.wireOp",EDGE,"E4.2.30.0");var subQ1=sQuery(id+"F0.wireOp",EDGE,"E0");var subQ2=makeQuery(id+"F0.imprint","INTERSECT",VERTEX,{"derivedFrom":[subQ1,subQ0]});Q61=makeQuery(id+"F0.imprint","IMPRINT",FACE,{"disambiguationData":[TD([[makeQuery(id+"F0.imprint","IMPRINT",EDGE,{"disambiguationData":[TD([[subQ2,1.0]])],"derivedFrom":subQ1}),-1.0]])]});}
            var Q62;
            {var subQ0=sQuery(id+"F0.wireOp",EDGE,"E4.2.15.0");var subQ1=sQuery(id+"F0.wireOp",EDGE,"E0");var subQ2=makeQuery(id+"F0.imprint","INTERSECT",VERTEX,{"derivedFrom":[subQ1,subQ0]});Q62=makeQuery(id+"F0.imprint","IMPRINT",FACE,{"disambiguationData":[TD([[makeQuery(id+"F0.imprint","IMPRINT",EDGE,{"disambiguationData":[TD([[subQ2,1.0]])],"derivedFrom":subQ1}),-1.0]])]});}
            var Q63;
            {var subQ0=sQuery(id+"F0.wireOp",EDGE,"E4.2.14.0");var subQ1=sQuery(id+"F0.wireOp",EDGE,"E0");var subQ2=makeQuery(id+"F0.imprint","INTERSECT",VERTEX,{"derivedFrom":[subQ1,subQ0]});Q63=makeQuery(id+"F0.imprint","IMPRINT",FACE,{"disambiguationData":[TD([[makeQuery(id+"F0.imprint","IMPRINT",EDGE,{"disambiguationData":[TD([[subQ2,1.0]])],"derivedFrom":subQ1}),-1.0]])]});}
            var Q64;
            {var subQ0=sQuery(id+"F0.wireOp",EDGE,"E4.2.9.0");var subQ1=sQuery(id+"F0.wireOp",EDGE,"E0");var subQ2=makeQuery(id+"F0.imprint","INTERSECT",VERTEX,{"derivedFrom":[subQ1,subQ0]});Q64=makeQuery(id+"F0.imprint","IMPRINT",FACE,{"disambiguationData":[TD([[makeQuery(id+"F0.imprint","IMPRINT",EDGE,{"disambiguationData":[TD([[subQ2,1.0]])],"derivedFrom":subQ1}),-1.0]])]});}
            extrude(context, id + "F1", {"entities" : qUnion([Q0, Q1, Q2, Q3, Q4, Q5, Q6, Q7, Q8, Q9, Q10, Q11, Q12, Q13, Q14, Q15, Q16, Q17, Q18, Q19, Q20, Q21, Q22, Q23, Q24, Q25, Q26, Q27, Q28, Q29, Q30, Q31, Q32, Q33, Q34, Q35, Q36, Q37, Q38, Q39, Q40, Q41, Q42, Q43, Q44, Q45, Q46, Q47, Q48, Q49, Q50, Q51, Q52, Q53, Q54, Q55, Q56, Q57, Q58, Q59, Q60, Q61, Q62, Q63, Q64]), "depth" : 5.08 * mm});
        }
        {
            var Q0;
            Q0=makeQuery(id+"F1.opExtrude","CAP_FACE",FACE,{"disambiguationData":[OSD([sQuery(id+"F0.wireOp",EDGE,"E1"),sQuery(id+"F0.wireOp",EDGE,"E2"),sQuery(id+"F0.wireOp",EDGE,"E3.1.0"),sQuery(id+"F0.wireOp",EDGE,"E3.1.1"),sQuery(id+"F0.wireOp",EDGE,"E3.2.0"),sQuery(id+"F0.wireOp",EDGE,"E3.2.1"),sQuery(id+"F0.wireOp",EDGE,"E4.2.3.0"),sQuery(id+"F0.wireOp",EDGE,"E4.3.3.0"),sQuery(id+"F0.wireOp",EDGE,"E4.2.4.0"),sQuery(id+"F0.wireOp",EDGE,"E4.3.4.0"),sQuery(id+"F0.wireOp",EDGE,"E4.2.5.0"),sQuery(id+"F0.wireOp",EDGE,"E4.3.5.0"),sQuery(id+"F0.wireOp",EDGE,"E4.2.6.0"),sQuery(id+"F0.wireOp",EDGE,"E4.3.6.0"),sQuery(id+"F0.wireOp",EDGE,"E4.2.7.0"),sQuery(id+"F0.wireOp",EDGE,"E4.3.7.0"),sQuery(id+"F0.wireOp",EDGE,"E4.2.8.0"),sQuery(id+"F0.wireOp",EDGE,"E4.3.8.0"),sQuery(id+"F0.wireOp",EDGE,"E4.2.9.0"),sQuery(id+"F0.wireOp",EDGE,"E4.3.9.0"),sQuery(id+"F0.wireOp",EDGE,"E4.2.10.0"),sQuery(id+"F0.wireOp",EDGE,"E4.3.10.0"),sQuery(id+"F0.wireOp",EDGE,"E4.2.11.0"),sQuery(id+"F0.wireOp",EDGE,"E4.3.11.0"),sQuery(id+"F0.wireOp",EDGE,"E4.2.12.0"),sQuery(id+"F0.wireOp",EDGE,"E4.3.12.0"),sQuery(id+"F0.wireOp",EDGE,"E4.2.13.0"),sQuery(id+"F0.wireOp",EDGE,"E4.3.13.0"),sQuery(id+"F0.wireOp",EDGE,"E4.2.14.0"),sQuery(id+"F0.wireOp",EDGE,"E4.3.14.0"),sQuery(id+"F0.wireOp",EDGE,"E4.2.15.0"),sQuery(id+"F0.wireOp",EDGE,"E4.3.15.0"),sQuery(id+"F0.wireOp",EDGE,"E4.2.16.0"),sQuery(id+"F0.wireOp",EDGE,"E4.3.16.0"),sQuery(id+"F0.wireOp",EDGE,"E4.2.17.0"),sQuery(id+"F0.wireOp",EDGE,"E4.3.17.0"),sQuery(id+"F0.wireOp",EDGE,"E4.2.18.0"),sQuery(id+"F0.wireOp",EDGE,"E4.3.18.0"),sQuery(id+"F0.wireOp",EDGE,"E4.2.19.0"),sQuery(id+"F0.wireOp",EDGE,"E4.3.19.0"),sQuery(id+"F0.wireOp",EDGE,"E4.2.20.0"),sQuery(id+"F0.wireOp",EDGE,"E4.3.20.0"),sQuery(id+"F0.wireOp",EDGE,"E4.2.21.0"),sQuery(id+"F0.wireOp",EDGE,"E4.3.21.0"),sQuery(id+"F0.wireOp",EDGE,"E4.2.22.0"),sQuery(id+"F0.wireOp",EDGE,"E4.3.22.0"),sQuery(id+"F0.wireOp",EDGE,"E4.2.23.0"),sQuery(id+"F0.wireOp",EDGE,"E4.3.23.0"),sQuery(id+"F0.wireOp",EDGE,"E4.2.24.0"),sQuery(id+"F0.wireOp",EDGE,"E4.3.24.0"),sQuery(id+"F0.wireOp",EDGE,"E4.2.25.0"),sQuery(id+"F0.wireOp",EDGE,"E4.3.25.0"),sQuery(id+"F0.wireOp",EDGE,"E4.2.26.0"),sQuery(id+"F0.wireOp",EDGE,"E4.3.26.0"),sQuery(id+"F0.wireOp",EDGE,"E4.2.27.0"),sQuery(id+"F0.wireOp",EDGE,"E4.3.27.0"),sQuery(id+"F0.wireOp",EDGE,"E4.2.28.0"),sQuery(id+"F0.wireOp",EDGE,"E4.3.28.0"),sQuery(id+"F0.wireOp",EDGE,"E4.2.29.0"),sQuery(id+"F0.wireOp",EDGE,"E4.3.29.0"),sQuery(id+"F0.wireOp",EDGE,"E4.2.30.0"),sQuery(id+"F0.wireOp",EDGE,"E4.3.30.0"),sQuery(id+"F0.wireOp",EDGE,"E4.2.31.0"),sQuery(id+"F0.wireOp",EDGE,"E4.3.31.0")])],"isStart":false});
            var sketch = newSketch(context, id + "F2", { "sketchPlane" : qUnion([Q0])});
            skCircle(sketch, "E5", {"center": v(0, 0) * mm, "radius": 1.52 * mm});
            skSolve(sketch);
        }
        {
            var Q0;
            Q0=makeQuery(id+"F2.imprint","IMPRINT",FACE,{"disambiguationData":[TD([[makeQuery(id+"F2.imprint","IMPRINT",EDGE,{"derivedFrom":sQuery(id+"F2.wireOp",EDGE,"E5")}),1.0]])]});
            extrude(context, id + "F3", {"entities" : qUnion([Q0]), "operationType" : NewBodyOperationType.REMOVE, "oppositeDirection" : true, "depth" : 5.08 * mm});
        }
        {
            var Q0;
            Q0=makeQuery(id+"F1.opExtrude","CAP_FACE",FACE,{"disambiguationData":[OSD([sQuery(id+"F0.wireOp",EDGE,"E1"),sQuery(id+"F0.wireOp",EDGE,"E2"),sQuery(id+"F0.wireOp",EDGE,"E3.1.0"),sQuery(id+"F0.wireOp",EDGE,"E3.1.1"),sQuery(id+"F0.wireOp",EDGE,"E3.2.0"),sQuery(id+"F0.wireOp",EDGE,"E3.2.1"),sQuery(id+"F0.wireOp",EDGE,"E4.2.3.0"),sQuery(id+"F0.wireOp",EDGE,"E4.3.3.0"),sQuery(id+"F0.wireOp",EDGE,"E4.2.4.0"),sQuery(id+"F0.wireOp",EDGE,"E4.3.4.0"),sQuery(id+"F0.wireOp",EDGE,"E4.2.5.0"),sQuery(id+"F0.wireOp",EDGE,"E4.3.5.0"),sQuery(id+"F0.wireOp",EDGE,"E4.2.6.0"),sQuery(id+"F0.wireOp",EDGE,"E4.3.6.0"),sQuery(id+"F0.wireOp",EDGE,"E4.2.7.0"),sQuery(id+"F0.wireOp",EDGE,"E4.3.7.0"),sQuery(id+"F0.wireOp",EDGE,"E4.2.8.0"),sQuery(id+"F0.wireOp",EDGE,"E4.3.8.0"),sQuery(id+"F0.wireOp",EDGE,"E4.2.9.0"),sQuery(id+"F0.wireOp",EDGE,"E4.3.9.0"),sQuery(id+"F0.wireOp",EDGE,"E4.2.10.0"),sQuery(id+"F0.wireOp",EDGE,"E4.3.10.0"),sQuery(id+"F0.wireOp",EDGE,"E4.2.11.0"),sQuery(id+"F0.wireOp",EDGE,"E4.3.11.0"),sQuery(id+"F0.wireOp",EDGE,"E4.2.12.0"),sQuery(id+"F0.wireOp",EDGE,"E4.3.12.0"),sQuery(id+"F0.wireOp",EDGE,"E4.2.13.0"),sQuery(id+"F0.wireOp",EDGE,"E4.3.13.0"),sQuery(id+"F0.wireOp",EDGE,"E4.2.14.0"),sQuery(id+"F0.wireOp",EDGE,"E4.3.14.0"),sQuery(id+"F0.wireOp",EDGE,"E4.2.15.0"),sQuery(id+"F0.wireOp",EDGE,"E4.3.15.0"),sQuery(id+"F0.wireOp",EDGE,"E4.2.16.0"),sQuery(id+"F0.wireOp",EDGE,"E4.3.16.0"),sQuery(id+"F0.wireOp",EDGE,"E4.2.17.0"),sQuery(id+"F0.wireOp",EDGE,"E4.3.17.0"),sQuery(id+"F0.wireOp",EDGE,"E4.2.18.0"),sQuery(id+"F0.wireOp",EDGE,"E4.3.18.0"),sQuery(id+"F0.wireOp",EDGE,"E4.2.19.0"),sQuery(id+"F0.wireOp",EDGE,"E4.3.19.0"),sQuery(id+"F0.wireOp",EDGE,"E4.2.20.0"),sQuery(id+"F0.wireOp",EDGE,"E4.3.20.0"),sQuery(id+"F0.wireOp",EDGE,"E4.2.21.0"),sQuery(id+"F0.wireOp",EDGE,"E4.3.21.0"),sQuery(id+"F0.wireOp",EDGE,"E4.2.22.0"),sQuery(id+"F0.wireOp",EDGE,"E4.3.22.0"),sQuery(id+"F0.wireOp",EDGE,"E4.2.23.0"),sQuery(id+"F0.wireOp",EDGE,"E4.3.23.0"),sQuery(id+"F0.wireOp",EDGE,"E4.2.24.0"),sQuery(id+"F0.wireOp",EDGE,"E4.3.24.0"),sQuery(id+"F0.wireOp",EDGE,"E4.2.25.0"),sQuery(id+"F0.wireOp",EDGE,"E4.3.25.0"),sQuery(id+"F0.wireOp",EDGE,"E4.2.26.0"),sQuery(id+"F0.wireOp",EDGE,"E4.3.26.0"),sQuery(id+"F0.wireOp",EDGE,"E4.2.27.0"),sQuery(id+"F0.wireOp",EDGE,"E4.3.27.0"),sQuery(id+"F0.wireOp",EDGE,"E4.2.28.0"),sQuery(id+"F0.wireOp",EDGE,"E4.3.28.0"),sQuery(id+"F0.wireOp",EDGE,"E4.2.29.0"),sQuery(id+"F0.wireOp",EDGE,"E4.3.29.0"),sQuery(id+"F0.wireOp",EDGE,"E4.2.30.0"),sQuery(id+"F0.wireOp",EDGE,"E4.3.30.0"),sQuery(id+"F0.wireOp",EDGE,"E4.2.31.0"),sQuery(id+"F0.wireOp",EDGE,"E4.3.31.0")])],"isStart":true});
            var sketch = newSketch(context, id + "F4", { "sketchPlane" : qUnion([Q0])});
            skCircle(sketch, "E6", {"center": v(0, 0) * mm, "radius": 3.17 * mm});
            skSolve(sketch);
        }
        {
            var Q0;
            Q0=makeQuery(id+"F4.imprint","IMPRINT",FACE,{"disambiguationData":[TD([[makeQuery(id+"F4.imprint","IMPRINT",EDGE,{"derivedFrom":sQuery(id+"F4.wireOp",EDGE,"E6")}),1.0]])]});
            extrude(context, id + "F5", {"entities" : qUnion([Q0]), "operationType" : NewBodyOperationType.ADD, "depth" : 3.8 * mm});
        }
    });
